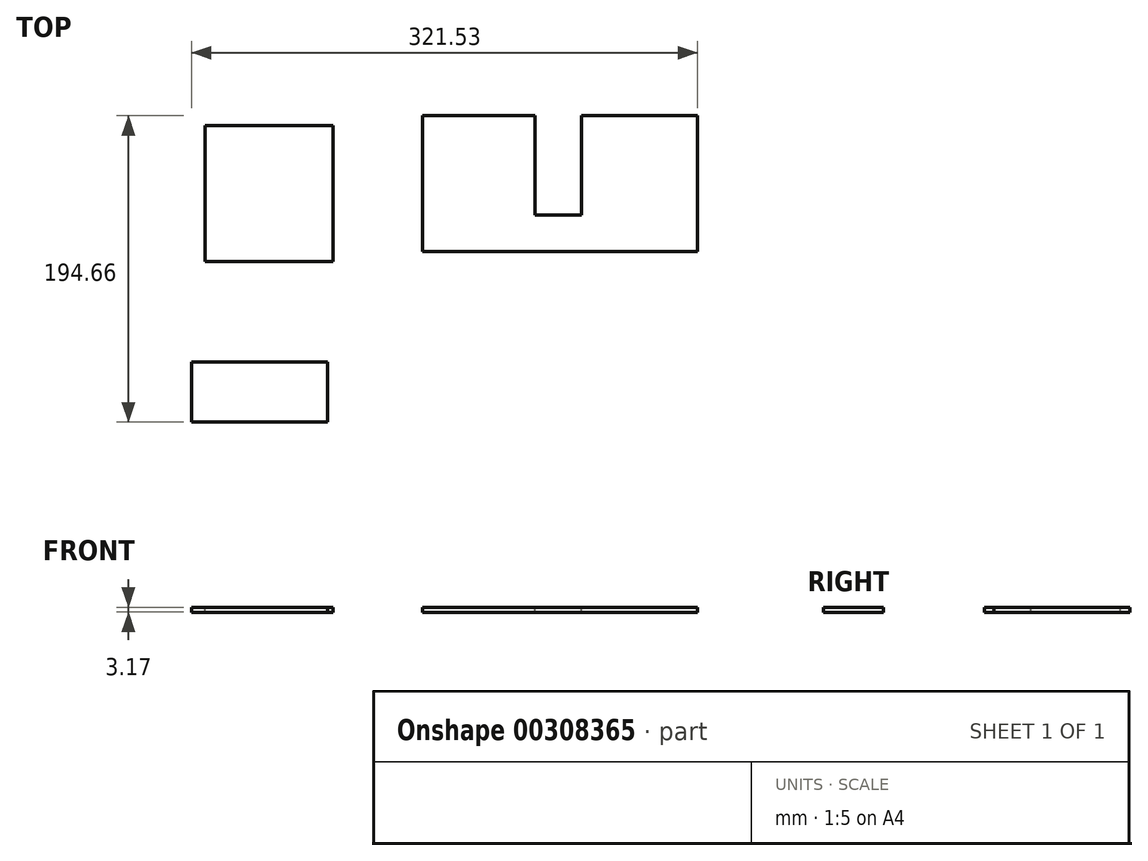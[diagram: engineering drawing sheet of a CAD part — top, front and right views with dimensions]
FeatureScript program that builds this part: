
annotation { "Feature Type Name" : "Feature", "Feature Type Description" : "" }
export const myFeature = defineFeature(function(context is Context, id is Id, definition is map)
    precondition{}
    {
        {
            var Q0;
            Q0=qCreatedBy(makeId("Top.planeOp"),FACE);
            var sketch = newSketch(context, id + "F0", { "sketchPlane" : qUnion([Q0])});
            skLineSegment(sketch, "E0.bottom", {"start": v(-106.58, 91.18) * mm, "end": v(-25.3, 91.18) * mm});
            skLineSegment(sketch, "E0.top", {"start": v(-106.58, 4.82) * mm, "end": v(-25.3, 4.82) * mm});
            skLineSegment(sketch, "E0.left", {"start": v(-106.58, 91.18) * mm, "end": v(-106.58, 4.82) * mm});
            skLineSegment(sketch, "E0.right", {"start": v(-25.3, 91.18) * mm, "end": v(-25.3, 4.82) * mm});
            skSolve(sketch);
        }
        {
            var Q0;
            Q0 = qSketchRegion(id + "F0", true);
            extrude(context, id + "F1", {"entities" : qUnion([Q0]), "oppositeDirection" : true, "depth" : 3.17 * mm});
        }
        {
            var Q0;
            Q0=qCreatedBy(makeId("Top.planeOp"),FACE);
            var sketch = newSketch(context, id + "F2", { "sketchPlane" : qUnion([Q0])});
            skLineSegment(sketch, "E1.bottom", {"start": v(-115.14, -59.24) * mm, "end": v(-28.78, -59.24) * mm});
            skLineSegment(sketch, "E1.top", {"start": v(-115.14, -97.34) * mm, "end": v(-28.78, -97.34) * mm});
            skLineSegment(sketch, "E1.left", {"start": v(-115.14, -59.24) * mm, "end": v(-115.14, -97.34) * mm});
            skLineSegment(sketch, "E1.right", {"start": v(-28.78, -59.24) * mm, "end": v(-28.78, -97.34) * mm});
            skSolve(sketch);
        }
        {
            var Q0;
            Q0 = qSketchRegion(id + "F2", true);
            extrude(context, id + "F3", {"entities" : qUnion([Q0]), "oppositeDirection" : true, "depth" : 3.17 * mm});
        }
        {
            var Q0;
            Q0=qCreatedBy(makeId("Top.planeOp"),FACE);
            var sketch = newSketch(context, id + "F4", { "sketchPlane" : qUnion([Q0])});
            skLineSegment(sketch, "E2.bottom", {"start": v(31.76, 97.32) * mm, "end": v(103.14, 97.32) * mm});
            skLineSegment(sketch, "E2.top", {"start": v(31.76, 10.96) * mm, "end": v(206.39, 10.96) * mm});
            skLineSegment(sketch, "E2.left", {"start": v(31.76, 97.32) * mm, "end": v(31.76, 10.96) * mm});
            skLineSegment(sketch, "E2.right", {"start": v(206.39, 97.32) * mm, "end": v(206.39, 10.96) * mm});
            skLineSegment(sketch, "E3.top", {"start": v(103.14, 34.32) * mm, "end": v(132.73, 34.32) * mm});
            skLineSegment(sketch, "E3.left", {"start": v(103.14, 97.32) * mm, "end": v(103.14, 34.32) * mm});
            skLineSegment(sketch, "E3.right", {"start": v(132.73, 97.32) * mm, "end": v(132.73, 34.32) * mm});
            skLineSegment(sketch, "E4.trimOffspring", {"start": v(132.73, 97.32) * mm, "end": v(206.39, 97.32) * mm});
            skSolve(sketch);
        }
        {
            var Q0;
            Q0 = qSketchRegion(id + "F4", true);
            extrude(context, id + "F5", {"entities" : qUnion([Q0]), "oppositeDirection" : true, "depth" : 3.17 * mm});
        }
    });
